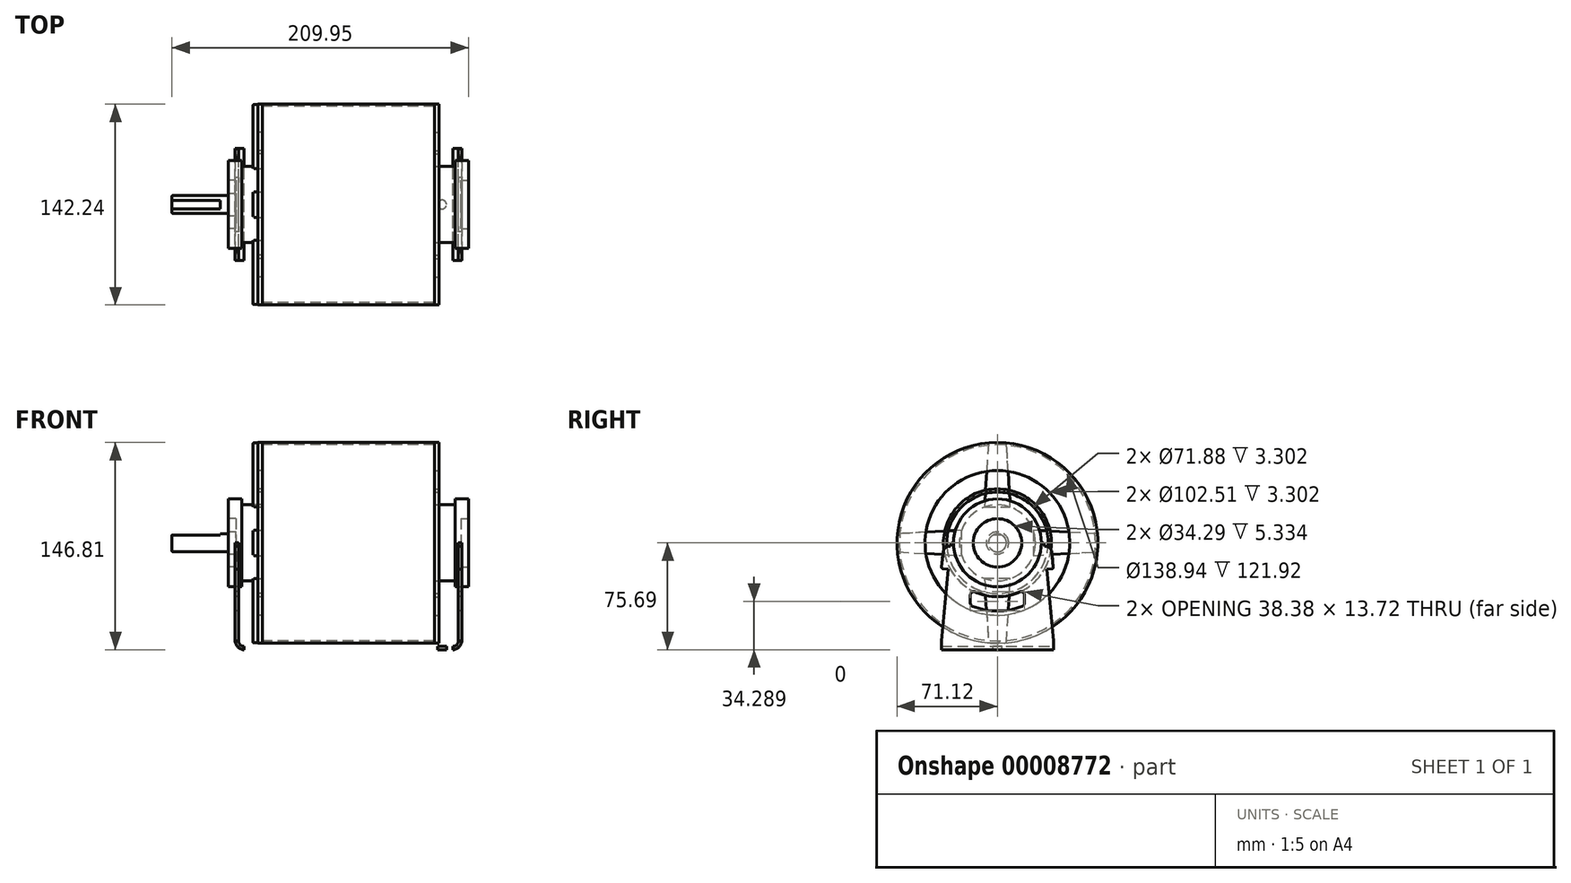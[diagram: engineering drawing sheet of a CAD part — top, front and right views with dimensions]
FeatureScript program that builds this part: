
annotation { "Feature Type Name" : "Feature", "Feature Type Description" : "" }
export const myFeature = defineFeature(function(context is Context, id is Id, definition is map)
    precondition{}
    {
        {
            var Q0;
            Q0=qCreatedBy(makeId("Right.planeOp"),FACE);
            var sketch = newSketch(context, id + "F0", { "sketchPlane" : qUnion([Q0])});
            skCircle(sketch, "E0", {"center": v(0, 0) * mm, "radius": 71.12 * mm});
            skCircle(sketch, "E1.0", {"center": v(0, 0) * mm, "radius": 69.47 * mm});
            skSolve(sketch);
        }
        {
            var Q0;
            Q0=makeQuery(id+"F0.imprint","IMPRINT",FACE,{"disambiguationData":[TD([[makeQuery(id+"F0.imprint","IMPRINT",EDGE,{"derivedFrom":sQuery(id+"F0.wireOp",EDGE,"E0")}),1.0]])]});
            extrude(context, id + "F1", {"entities" : qUnion([Q0]), "depth" : 121.92 * mm});
        }
        {
            var Q0;
            Q0=qCreatedBy(makeId("Front.planeOp"),FACE);
            var sketch = newSketch(context, id + "F2", { "sketchPlane" : qUnion([Q0])});
            skLineSegment(sketch, "E2", {"start": v(0, 0) * mm, "end": v(0, 71.12) * mm});
            skLineSegment(sketch, "E3", {"start": v(0, 71.12) * mm, "end": v(-3.3, 71.12) * mm});
            skLineSegment(sketch, "E4", {"start": v(-3.3, 71.12) * mm, "end": v(-3.3, 26.92) * mm});
            skLineSegment(sketch, "E5", {"start": v(-3.3, 26.92) * mm, "end": v(-14.48, 26.92) * mm});
            skLineSegment(sketch, "E6", {"start": v(-14.48, 26.92) * mm, "end": v(-14.48, 31.12) * mm});
            skLineSegment(sketch, "E7", {"start": v(-14.48, 31.12) * mm, "end": v(-24, 31.12) * mm});
            skLineSegment(sketch, "E8", {"start": v(-24, 31.12) * mm, "end": v(-24, 17.15) * mm});
            skLineSegment(sketch, "E9", {"start": v(-24, 17.15) * mm, "end": v(-18.67, 17.15) * mm});
            skLineSegment(sketch, "E10", {"start": v(-18.67, 17.15) * mm, "end": v(-18.67, 0) * mm});
            skLineSegment(sketch, "E11", {"start": v(-18.67, 0) * mm, "end": v(0, 0) * mm});
            skSolve(sketch);
        }
        {
            var Q0;
            Q0=makeQuery(id+"F2.imprint","IMPRINT",FACE,{"disambiguationData":[TD([[makeQuery(id+"F2.imprint","IMPRINT",EDGE,{"derivedFrom":sQuery(id+"F2.wireOp",EDGE,"E2")}),1.0]])]});
            var Q1;
            Q1=sQuery(id+"F2.wireOp",EDGE,"E11");
            revolve(context, id + "F3", {"entities" : qUnion([Q0]), "axis" : qUnion([Q1]), "revolveType" : RevolveType.FULL});
        }
        {
            var Q0;
            Q0=makeQuery(id+"F3.opRevolve","SWEPT_FACE",FACE,{"disambiguationData":[OSD([sQuery(id+"F2.wireOp",EDGE,"E4")])]});
            var sketch = newSketch(context, id + "F4", { "sketchPlane" : qUnion([Q0])});
            skCircle(sketch, "E12", {"center": v(0, 0) * mm, "radius": 51.26 * mm});
            skCircle(sketch, "E13", {"center": v(0, 0) * mm, "radius": 38.23 * mm});
            skCircle(sketch, "E14.0", {"center": v(0, 0) * mm, "radius": 35.94 * mm});
            skSolve(sketch);
        }
        {
            var Q0;
            Q0 = qSketchRegion(id + "F4", true);
            var Q1;
            Q1=makeQuery(id+"F4.imprint","IMPRINT",FACE,{"disambiguationData":[TD([[makeQuery(id+"F4.imprint","IMPRINT",EDGE,{"derivedFrom":sQuery(id+"F4.wireOp",EDGE,"E14.0")}),1.0]])]});
            extrude(context, id + "F5", {"entities" : qUnion([Q0, Q1]), "operationType" : NewBodyOperationType.REMOVE, "endBound" : BoundingType.THROUGH_ALL, "oppositeDirection" : true, "depth" : 25.4 * mm});
        }
        {
            var Q0;
            Q0=qCreatedBy(makeId("Right.planeOp"),FACE);
            var sketch = newSketch(context, id + "F6", { "sketchPlane" : qUnion([Q0])});
            skLineSegment(sketch, "E15", {"start": v(0, 0) * mm, "end": v(0, 71.12) * mm, "construction": true});
            skPoint(sketch, "E16.rect.middle", {"position": v(0, 71.12) * mm});
            skCircle(sketch, "E17", {"center": v(0, 26.92) * mm, "radius": 9.2 * mm, "construction": true});
            skCircle(sketch, "E18.0", {"center": v(0, 0) * mm, "radius": 71.12 * mm, "construction": true});
            skCircle(sketch, "E19", {"center": v(0, 71.12) * mm, "radius": 6.35 * mm, "construction": true});
            skLineSegment(sketch, "E20", {"start": v(9.07, 25.35) * mm, "end": v(6.38, 70.83) * mm});
            skLineSegment(sketch, "E21", {"start": v(6.38, 70.83) * mm, "end": v(-6.38, 70.83) * mm});
            skLineSegment(sketch, "E22", {"start": v(-6.38, 70.83) * mm, "end": v(-9.07, 25.35) * mm});
            skLineSegment(sketch, "E23", {"start": v(-9.07, 25.35) * mm, "end": v(9.07, 25.35) * mm});
            skCircle(sketch, "E24.0", {"center": v(0, 0) * mm, "radius": 26.92 * mm, "construction": true});
            skSolve(sketch);
        }
        {
            var Q0;
            {var subQ3=sQuery(id+"F6.wireOp",EDGE,"E20");Q0=makeQuery(id+"F6.imprint","IMPRINT",FACE,{"disambiguationData":[TD([[makeQuery(id+"F6.imprint","IMPRINT",EDGE,{"derivedFrom":subQ3}),1.0]])]});}
            extrude(context, id + "F7", {"entities" : qUnion([Q0]), "oppositeDirection" : true, "depth" : 6.6 * mm});
        }
        {
            var Q0;
            Q0=makeQuery(id+"F7.opExtrude","CAP_EDGE",EDGE,{"disambiguationData":[OSD([sQuery(id+"F6.wireOp",EDGE,"E20")])],"isStart":false});
            var Q1;
            Q1=makeQuery(id+"F7.opExtrude","CAP_EDGE",EDGE,{"disambiguationData":[OSD([sQuery(id+"F6.wireOp",EDGE,"E21")])],"isStart":false});
            var Q2;
            Q2=makeQuery(id+"F7.opExtrude","CAP_EDGE",EDGE,{"disambiguationData":[OSD([sQuery(id+"F6.wireOp",EDGE,"E22")])],"isStart":false});
            var Q3;
            Q3=makeQuery(id+"F7.opExtrude","SWEPT_EDGE",EDGE,{"disambiguationData":[OSD([sQuery(id+"F2.wireOp",EDGE,"E3"),sQuery(id+"F2.wireOp",EDGE,"E4"),sQuery(id+"F6.wireOp",EDGE,"E20"),sQuery(id+"F6.wireOp",EDGE,"E21")])]});
            var Q4;
            Q4=makeQuery(id+"F7.opExtrude","SWEPT_EDGE",EDGE,{"disambiguationData":[OSD([sQuery(id+"F2.wireOp",EDGE,"E3"),sQuery(id+"F2.wireOp",EDGE,"E4"),sQuery(id+"F6.wireOp",EDGE,"E21"),sQuery(id+"F6.wireOp",EDGE,"E22")])]});
            fillet(context, id + "F8", {"entities" : qUnion([Q0, Q1, Q2, Q3, Q4]), "radius" : 0.5 * mm, "tangentPropagation" : true, "allowEdgeOverflow" : false});
        }
        {
            var Q0;
            Q0=makeQuery(id+"F7.opExtrude","SWEPT_BODY",BODY,{"disambiguationData":[OSD([sQuery(id+"F2.wireOp",EDGE,"E4"),sQuery(id+"F2.wireOp",EDGE,"E5"),sQuery(id+"F6.wireOp",EDGE,"E20"),sQuery(id+"F6.wireOp",EDGE,"E21"),sQuery(id+"F6.wireOp",EDGE,"E22")])]});
            var Q1;
            Q1=sQuery(id+"F2.wireOp",EDGE,"E11");
            circularPattern(context, id + "F9", {"entities" : qUnion([Q0]), "axis" : qUnion([Q1]), "angle" : 360 * degree, "instanceCount" : 4, "equalSpace" : true});
        }
        {
            var Q0;
            Q0=qCreatedBy(makeId("Right.planeOp"),FACE);
            cPlane(context, id + "F10", {"entities" : qUnion([Q0]), "cplaneType" : CPlaneType.OFFSET, "offset" : 60.96 * mm, "width" : 152.4 * mm, "height" : 152.4 * mm});
        }
        {
            var Q0;
            Q0=makeQuery(id+"F5.boolean.opBoolean","SPLIT",BODY,{"disambiguationData":[OD(0.0)],"derivedFrom":makeQuery(id+"F3.opRevolve","SWEPT_BODY",BODY,{"disambiguationData":[OSD([sQuery(id+"F2.wireOp",EDGE,"E2"),sQuery(id+"F2.wireOp",EDGE,"E3"),sQuery(id+"F2.wireOp",EDGE,"E4"),sQuery(id+"F2.wireOp",EDGE,"E5"),sQuery(id+"F2.wireOp",EDGE,"E6"),sQuery(id+"F2.wireOp",EDGE,"E7"),sQuery(id+"F2.wireOp",EDGE,"E8"),sQuery(id+"F2.wireOp",EDGE,"E9"),sQuery(id+"F2.wireOp",EDGE,"E10"),sQuery(id+"F2.wireOp",EDGE,"E11")])]})});
            var Q1;
            Q1=qCreatedBy(id+"F10.planeOp",FACE);
            mirror(context, id + "F11", {"entities" : qUnion([Q0]), "mirrorPlane" : qUnion([Q1])});
        }
        {
            var Q0;
            Q0=qCreatedBy(makeId("Front.planeOp"),FACE);
            var sketch = newSketch(context, id + "F12", { "sketchPlane" : qUnion([Q0])});
            skLineSegment(sketch, "E25.0.0", {"start": v(-18.67, -17.15) * mm, "end": v(-18.67, 17.15) * mm, "construction": true});
            skLineSegment(sketch, "E26", {"start": v(-18.67, 0) * mm, "end": v(-64.03, 0) * mm});
            skLineSegment(sketch, "E27", {"start": v(-64.03, 0) * mm, "end": v(-64.03, 5.84) * mm});
            skLineSegment(sketch, "E28", {"start": v(-63.53, 6.35) * mm, "end": v(-23.75, 6.35) * mm});
            skLineSegment(sketch, "E29", {"start": v(-23.24, 7.89) * mm, "end": v(-18.67, 7.89) * mm});
            skLineSegment(sketch, "E30", {"start": v(-18.67, 7.89) * mm, "end": v(-18.67, 0) * mm});
            skLineSegment(sketch, "E31", {"start": v(-23.75, 7.38) * mm, "end": v(-23.75, 6.35) * mm});
            skPoint(sketch, "E32.visualSharp", {"position": v(-23.75, 7.89) * mm});
            skArc(sketch, "E32.filletArc", {"start": v(-23.24, 7.89) * mm, "mid": v(-23.6, 7.74) * mm, "end": v(-23.75, 7.38) * mm});
            skPoint(sketch, "E33.visualSharp", {"position": v(-64.03, 6.35) * mm});
            skArc(sketch, "E33.filletArc", {"start": v(-63.53, 6.35) * mm, "mid": v(-63.88, 6.2) * mm, "end": v(-64.03, 5.84) * mm});
            skSolve(sketch);
        }
        {
            var Q0;
            Q0=makeQuery(id+"F12.imprint","IMPRINT",FACE,{"disambiguationData":[TD([[makeQuery(id+"F12.imprint","IMPRINT",EDGE,{"derivedFrom":sQuery(id+"F12.wireOp",EDGE,"E26")}),-1.0]])]});
            var Q1;
            Q1=sQuery(id+"F12.wireOp",EDGE,"E26");
            revolve(context, id + "F13", {"entities" : qUnion([Q0]), "axis" : qUnion([Q1]), "revolveType" : RevolveType.FULL});
        }
        {
            var Q0;
            Q0=makeQuery(id+"F13.opRevolve","SWEPT_FACE",FACE,{"disambiguationData":[OSD([sQuery(id+"F12.wireOp",EDGE,"E27")])]});
            var sketch = newSketch(context, id + "F14", { "sketchPlane" : qUnion([Q0])});
            skCircle(sketch, "E34.0", {"center": v(0, 0) * mm, "radius": 6.35 * mm});
            skLineSegment(sketch, "E35", {"start": v(-6.6, -6.35) * mm, "end": v(6.6, -6.35) * mm, "construction": true});
            skLineSegment(sketch, "E36", {"start": v(0, -6.35) * mm, "end": v(0, 6.35) * mm, "construction": true});
            skLineSegment(sketch, "E37.0", {"start": v(-3.02, 5.59) * mm, "end": v(3.02, 5.59) * mm});
            skSolve(sketch);
        }
        {
            var Q0;
            {var subQ0=makeQuery(id+"F13.opRevolve","SWEPT_EDGE",EDGE,{"disambiguationData":[OSD([sQuery(id+"F12.wireOp",EDGE,"E27"),sQuery(id+"F12.wireOp",EDGE,"E33.filletArc")])]});var subQ1=sQuery(id+"F14.wireOp",EDGE,"E37.0");var subQ3=makeQuery(id+"F14.imprint","INTERSECT",VERTEX,{"disambiguationData":[OD(0.0)],"derivedFrom":[subQ0,subQ1]});Q0=makeQuery(id+"F14.imprint","IMPRINT",FACE,{"disambiguationData":[TD([[makeQuery(id+"F14.imprint","IMPRINT",EDGE,{"disambiguationData":[TD([[subQ3,-1.0]])],"derivedFrom":subQ1}),1.0]])]});}
            var Q1;
            {var subQ1=sQuery(id+"F14.wireOp",EDGE,"E37.0");var subQ4=sQuery(id+"F14.wireOp",EDGE,"E34.0");var subQ6=makeQuery(id+"F14.imprint","INTERSECT",VERTEX,{"disambiguationData":[OD(0.0)],"derivedFrom":[subQ4,subQ1]});Q1=makeQuery(id+"F14.imprint","IMPRINT",FACE,{"disambiguationData":[TD([[makeQuery(id+"F14.imprint","IMPRINT",EDGE,{"disambiguationData":[TD([[subQ6,1.0]])],"derivedFrom":subQ4}),1.0]])]});}
            extrude(context, id + "F15", {"entities" : qUnion([Q0, Q1]), "operationType" : NewBodyOperationType.REMOVE, "oppositeDirection" : true, "depth" : 34.04 * mm});
        }
        {
            var Q0;
            Q0=qCreatedBy(makeId("Front.planeOp"),FACE);
            var sketch = newSketch(context, id + "F16", { "sketchPlane" : qUnion([Q0])});
            skLineSegment(sketch, "E38", {"start": v(-154.25, 0) * mm, "end": v(252.33, 0) * mm, "construction": true});
            skLineSegment(sketch, "E39", {"start": v(-12.9, -75.7) * mm, "end": v(134.81, -75.7) * mm});
            skLineSegment(sketch, "E40", {"start": v(-24, 31.12) * mm, "end": v(-14.48, 31.12) * mm, "construction": true});
            skLineSegment(sketch, "E41", {"start": v(136.4, 31.12) * mm, "end": v(145.92, 31.12) * mm, "construction": true});
            skLineSegment(sketch, "E42", {"start": v(-19.24, 31.12) * mm, "end": v(-19.24, 0) * mm, "construction": true});
            skLineSegment(sketch, "E43", {"start": v(141.16, 31.12) * mm, "end": v(141.16, 0) * mm, "construction": true});
            skLineSegment(sketch, "E44", {"start": v(-19.24, 0) * mm, "end": v(-19.24, -69.34) * mm});
            skLineSegment(sketch, "E45", {"start": v(141.16, 0) * mm, "end": v(141.16, -69.34) * mm});
            skPoint(sketch, "E46.visualSharp", {"position": v(-19.24, -75.7) * mm});
            skArc(sketch, "E46.filletArc", {"start": v(-19.24, -69.34) * mm, "mid": v(-17.38, -73.83) * mm, "end": v(-12.9, -75.7) * mm});
            skPoint(sketch, "E47.visualSharp", {"position": v(141.16, -75.7) * mm});
            skArc(sketch, "E47.filletArc", {"start": v(134.81, -75.7) * mm, "mid": v(139.3, -73.83) * mm, "end": v(141.16, -69.34) * mm});
            skLineSegment(sketch, "E48.0", {"start": v(138.87, 0) * mm, "end": v(138.87, -69.34) * mm});
            skArc(sketch, "E48.1", {"start": v(134.81, -73.4) * mm, "mid": v(137.68, -72.22) * mm, "end": v(138.87, -69.34) * mm});
            skLineSegment(sketch, "E48.2", {"start": v(-12.9, -73.4) * mm, "end": v(134.81, -73.4) * mm});
            skArc(sketch, "E48.3", {"start": v(-16.95, -69.34) * mm, "mid": v(-15.76, -72.22) * mm, "end": v(-12.9, -73.4) * mm});
            skLineSegment(sketch, "E48.4", {"start": v(-16.95, 0) * mm, "end": v(-16.95, -69.34) * mm});
            skLineSegment(sketch, "E49", {"start": v(-19.24, 0) * mm, "end": v(-16.95, 0) * mm});
            skLineSegment(sketch, "E50", {"start": v(138.87, 0) * mm, "end": v(141.16, 0) * mm});
            skSolve(sketch);
        }
        {
            var Q0;
            Q0 = qSketchRegion(id + "F16", true);
            extrude(context, id + "F17", {"entities" : qUnion([Q0]), "depth" : 79.5 * mm, "symmetric" : true});
        }
        {
            var Q0;
            Q0=qCreatedBy(makeId("Top.planeOp"),FACE);
            cPlane(context, id + "F18", {"entities" : qUnion([Q0]), "cplaneType" : CPlaneType.OFFSET, "offset" : 75.7 * mm, "oppositeDirection" : true, "width" : 152.4 * mm, "height" : 152.4 * mm});
        }
        {
            var Q0;
            Q0=qCreatedBy(id+"F18.planeOp",FACE);
            var sketch = newSketch(context, id + "F19", { "sketchPlane" : qUnion([Q0])});
            skLineSegment(sketch, "E51.0", {"start": v(-19.24, -39.75) * mm, "end": v(-12.9, -39.75) * mm, "construction": true});
            skLineSegment(sketch, "E52.0", {"start": v(-19.24, 39.75) * mm, "end": v(-12.9, 39.75) * mm, "construction": true});
            skLineSegment(sketch, "E53.bottom", {"start": v(15.34, 66.04) * mm, "end": v(15.34, 66.04) * mm});
            skLineSegment(sketch, "E53.top", {"start": v(15.34, 40.64) * mm, "end": v(15.34, 40.64) * mm});
            skLineSegment(sketch, "E53.left", {"start": v(11.37, 62.07) * mm, "end": v(11.37, 44.6) * mm});
            skLineSegment(sketch, "E53.right", {"start": v(19.3, 62.07) * mm, "end": v(19.3, 44.6) * mm});
            skPoint(sketch, "E54.visualSharp", {"position": v(11.37, 66.04) * mm});
            skArc(sketch, "E54.filletArc", {"start": v(15.34, 66.04) * mm, "mid": v(12.53, 64.88) * mm, "end": v(11.37, 62.07) * mm});
            skPoint(sketch, "E55.visualSharp", {"position": v(19.3, 66.04) * mm});
            skArc(sketch, "E55.filletArc", {"start": v(19.3, 62.07) * mm, "mid": v(18.14, 64.88) * mm, "end": v(15.34, 66.04) * mm});
            skPoint(sketch, "E56.visualSharp", {"position": v(19.3, 40.64) * mm});
            skArc(sketch, "E56.filletArc", {"start": v(15.34, 40.64) * mm, "mid": v(18.14, 41.8) * mm, "end": v(19.3, 44.6) * mm});
            skPoint(sketch, "E57.visualSharp", {"position": v(11.37, 40.64) * mm});
            skArc(sketch, "E57.filletArc", {"start": v(11.37, 44.6) * mm, "mid": v(12.53, 41.8) * mm, "end": v(15.34, 40.64) * mm});
            skLineSegment(sketch, "E58", {"start": v(2.98, 39.75) * mm, "end": v(2.98, -39.75) * mm, "construction": true});
            skLineSegment(sketch, "E59", {"start": v(-19.24, 0) * mm, "end": v(141.16, 0) * mm, "construction": true});
            skLineSegment(sketch, "E60", {"start": v(9.33, 71.5) * mm, "end": v(111.68, 71.5) * mm});
            skLineSegment(sketch, "E61", {"start": v(9.33, -71.5) * mm, "end": v(111.68, -71.5) * mm});
            skLineSegment(sketch, "E62", {"start": v(2.98, 46.1) * mm, "end": v(2.98, 65.15) * mm});
            skLineSegment(sketch, "E63", {"start": v(2.98, -46.1) * mm, "end": v(2.98, -65.15) * mm});
            skLineSegment(sketch, "E64", {"start": v(-19.24, 39.75) * mm, "end": v(-19.24, -39.75) * mm, "construction": true});
            skLineSegment(sketch, "E65.0", {"start": v(141.16, -39.75) * mm, "end": v(141.16, 39.75) * mm, "construction": true});
            skLineSegment(sketch, "E66", {"start": v(141.16, 39.75) * mm, "end": v(134.81, 39.75) * mm, "construction": true});
            skLineSegment(sketch, "E67", {"start": v(126.25, 45.4) * mm, "end": v(117.6, 67.47) * mm});
            skPoint(sketch, "E68.visualSharp", {"position": v(128.46, 39.75) * mm});
            skArc(sketch, "E68.filletArc", {"start": v(126.25, 45.4) * mm, "mid": v(129.51, 41.3) * mm, "end": v(134.52, 39.75) * mm});
            skPoint(sketch, "E69.visualSharp", {"position": v(2.98, 71.5) * mm});
            skArc(sketch, "E69.filletArc", {"start": v(9.33, 71.5) * mm, "mid": v(4.84, 69.64) * mm, "end": v(2.98, 65.15) * mm});
            skLineSegment(sketch, "E70.0.MirrorCS", {"start": v(141.16, -39.75) * mm, "end": v(134.81, -39.75) * mm, "construction": true});
            skLineSegment(sketch, "E70.1.MirrorCS", {"start": v(126.25, -45.4) * mm, "end": v(117.6, -67.47) * mm});
            skArc(sketch, "E70.2.MirrorCS", {"start": v(126.25, -45.4) * mm, "mid": v(129.51, -41.3) * mm, "end": v(134.52, -39.75) * mm});
            skPoint(sketch, "E71.visualSharp", {"position": v(116.01, 71.5) * mm});
            skArc(sketch, "E71.filletArc", {"start": v(117.6, 67.47) * mm, "mid": v(115.26, 70.4) * mm, "end": v(111.68, 71.5) * mm});
            skPoint(sketch, "E72.visualSharp", {"position": v(116.01, -71.5) * mm});
            skArc(sketch, "E72.filletArc", {"start": v(111.68, -71.5) * mm, "mid": v(115.26, -70.4) * mm, "end": v(117.6, -67.47) * mm});
            skPoint(sketch, "E73.visualSharp", {"position": v(2.98, -71.5) * mm});
            skArc(sketch, "E73.filletArc", {"start": v(2.98, -65.15) * mm, "mid": v(4.84, -69.64) * mm, "end": v(9.33, -71.5) * mm});
            skPoint(sketch, "E74.visualSharp", {"position": v(2.98, 39.75) * mm});
            skArc(sketch, "E74.filletArc", {"start": v(-3.37, 39.75) * mm, "mid": v(1.12, 41.61) * mm, "end": v(2.98, 46.1) * mm});
            skPoint(sketch, "E75.visualSharp", {"position": v(2.98, -39.75) * mm});
            skArc(sketch, "E75.filletArc", {"start": v(2.98, -46.1) * mm, "mid": v(1.12, -41.61) * mm, "end": v(-3.37, -39.75) * mm});
            skArc(sketch, "E76.0.1.0", {"start": v(15.34, -66.04) * mm, "mid": v(18.14, -64.88) * mm, "end": v(19.3, -62.07) * mm});
            skArc(sketch, "E76.0.1.1", {"start": v(11.37, -62.07) * mm, "mid": v(12.53, -64.88) * mm, "end": v(15.34, -66.04) * mm});
            skLineSegment(sketch, "E76.0.1.2", {"start": v(11.37, -44.6) * mm, "end": v(11.37, -62.07) * mm});
            skArc(sketch, "E76.0.1.3", {"start": v(15.34, -40.64) * mm, "mid": v(12.53, -41.8) * mm, "end": v(11.37, -44.6) * mm});
            skArc(sketch, "E76.0.1.4", {"start": v(19.3, -44.6) * mm, "mid": v(18.14, -41.8) * mm, "end": v(15.34, -40.64) * mm});
            skLineSegment(sketch, "E76.0.1.5", {"start": v(19.3, -44.6) * mm, "end": v(19.3, -62.07) * mm});
            skArc(sketch, "E76.1.0.0", {"start": v(83.92, 40.64) * mm, "mid": v(86.72, 41.8) * mm, "end": v(87.88, 44.6) * mm});
            skArc(sketch, "E76.1.0.1", {"start": v(79.95, 44.6) * mm, "mid": v(81.1, 41.8) * mm, "end": v(83.92, 40.64) * mm});
            skLineSegment(sketch, "E76.1.0.2", {"start": v(79.95, 62.07) * mm, "end": v(79.95, 44.6) * mm});
            skArc(sketch, "E76.1.0.3", {"start": v(83.92, 66.04) * mm, "mid": v(81.1, 64.88) * mm, "end": v(79.95, 62.07) * mm});
            skArc(sketch, "E76.1.0.4", {"start": v(87.88, 62.07) * mm, "mid": v(86.72, 64.88) * mm, "end": v(83.92, 66.04) * mm});
            skLineSegment(sketch, "E76.1.0.5", {"start": v(87.88, 62.07) * mm, "end": v(87.88, 44.6) * mm});
            skArc(sketch, "E76.1.1.0", {"start": v(83.92, -66.04) * mm, "mid": v(86.72, -64.88) * mm, "end": v(87.88, -62.07) * mm});
            skArc(sketch, "E76.1.1.1", {"start": v(79.95, -62.07) * mm, "mid": v(81.1, -64.88) * mm, "end": v(83.92, -66.04) * mm});
            skLineSegment(sketch, "E76.1.1.2", {"start": v(79.95, -44.6) * mm, "end": v(79.95, -62.07) * mm});
            skArc(sketch, "E76.1.1.3", {"start": v(83.92, -40.64) * mm, "mid": v(81.1, -41.8) * mm, "end": v(79.95, -44.6) * mm});
            skArc(sketch, "E76.1.1.4", {"start": v(87.88, -44.6) * mm, "mid": v(86.72, -41.8) * mm, "end": v(83.92, -40.64) * mm});
            skLineSegment(sketch, "E76.1.1.5", {"start": v(87.88, -44.6) * mm, "end": v(87.88, -62.07) * mm});
            skLineSegment(sketch, "E76.direction1", {"start": v(15.34, 40.64) * mm, "end": v(83.92, 40.64) * mm, "construction": true});
            skLineSegment(sketch, "E76.direction2", {"start": v(15.34, 40.64) * mm, "end": v(15.34, -66.04) * mm, "construction": true});
            skLineSegment(sketch, "E77.0", {"start": v(-12.9, -39.75) * mm, "end": v(-12.9, 39.75) * mm});
            skLineSegment(sketch, "E78.0", {"start": v(134.81, -39.75) * mm, "end": v(134.81, 39.75) * mm});
            skLineSegment(sketch, "E79", {"start": v(-12.9, 39.75) * mm, "end": v(-3.37, 39.75) * mm});
            skLineSegment(sketch, "E80", {"start": v(-12.9, -39.75) * mm, "end": v(-3.37, -39.75) * mm});
            skLineSegment(sketch, "E81", {"start": v(134.81, 39.75) * mm, "end": v(134.52, 39.75) * mm});
            skLineSegment(sketch, "E82", {"start": v(134.81, -39.75) * mm, "end": v(134.52, -39.75) * mm});
            skSolve(sketch);
        }
        {
            var Q0;
            Q0=makeQuery(id+"F19.imprint","IMPRINT",FACE,{"disambiguationData":[TD([[makeQuery(id+"F19.imprint","IMPRINT",EDGE,{"derivedFrom":sQuery(id+"F19.wireOp",EDGE,"E53.left")}),-1.0]])]});
            extrude(context, id + "F20", {"entities" : qUnion([Q0]), "operationType" : NewBodyOperationType.ADD, "depth" : 2.3 * mm});
        }
        {
            var Q0;
            Q0=makeQuery(id+"F17.opExtrude","SWEPT_FACE",FACE,{"disambiguationData":[OSD([sQuery(id+"F16.wireOp",EDGE,"E44")])]});
            var sketch = newSketch(context, id + "F21", { "sketchPlane" : qUnion([Q0])});
            skArc(sketch, "E83.0", {"start": v(-31.12, 0) * mm, "mid": v(0, -31.12) * mm, "end": v(31.12, 0) * mm});
            skLineSegment(sketch, "E84.0", {"start": v(39.75, -69.34) * mm, "end": v(-39.75, -69.34) * mm});
            skLineSegment(sketch, "E85", {"start": v(31.87, 0) * mm, "end": v(31.12, 0) * mm});
            skLineSegment(sketch, "E86", {"start": v(-33.13, -1.15) * mm, "end": v(-39.75, -69.34) * mm});
            skLineSegment(sketch, "E87", {"start": v(33.13, -1.15) * mm, "end": v(39.75, -69.34) * mm});
            skPoint(sketch, "E88.end.orphan", {"position": v(-39.75, 0) * mm});
            skPoint(sketch, "E89.0.start.orphan", {"position": v(39.75, 0) * mm});
            skLineSegment(sketch, "E90.trimOffspring", {"start": v(-31.12, 0) * mm, "end": v(-31.87, 0) * mm});
            skLineSegment(sketch, "E91", {"start": v(0, 0) * mm, "end": v(0, -69.34) * mm, "construction": true});
            skPoint(sketch, "E92.visualSharp", {"position": v(-33.02, 0) * mm});
            skArc(sketch, "E92.filletArc", {"start": v(-31.87, 0) * mm, "mid": v(-32.72, -0.33) * mm, "end": v(-33.13, -1.15) * mm});
            skPoint(sketch, "E93.visualSharp", {"position": v(33.02, 0) * mm});
            skArc(sketch, "E93.filletArc", {"start": v(33.13, -1.15) * mm, "mid": v(32.72, -0.33) * mm, "end": v(31.87, 0) * mm});
            skLineSegment(sketch, "E94.bottom", {"start": v(33.27, -2.6) * mm, "end": v(33.78, -2.55) * mm});
            skLineSegment(sketch, "E94.top", {"start": v(34.84, -18.78) * mm, "end": v(38.38, -18.44) * mm});
            skLineSegment(sketch, "E94.left", {"start": v(33.27, -2.6) * mm, "end": v(34.84, -18.78) * mm});
            skLineSegment(sketch, "E94.right", {"start": v(38.5, -6.43) * mm, "end": v(39.52, -17.05) * mm});
            skPoint(sketch, "E95.visualSharp", {"position": v(38.08, -2.13) * mm});
            skArc(sketch, "E95.filletArc", {"start": v(38.5, -6.43) * mm, "mid": v(36.94, -3.51) * mm, "end": v(33.78, -2.55) * mm});
            skPoint(sketch, "E96.visualSharp", {"position": v(39.65, -18.31) * mm});
            skArc(sketch, "E96.filletArc", {"start": v(38.38, -18.44) * mm, "mid": v(39.24, -17.98) * mm, "end": v(39.52, -17.05) * mm});
            skLineSegment(sketch, "E97.0.MirrorCS", {"start": v(-33.27, -2.6) * mm, "end": v(-33.78, -2.55) * mm});
            skArc(sketch, "E97.1.MirrorCS", {"start": v(-38.5, -6.43) * mm, "mid": v(-36.94, -3.51) * mm, "end": v(-33.78, -2.55) * mm});
            skLineSegment(sketch, "E97.2.MirrorCS", {"start": v(-34.84, -18.78) * mm, "end": v(-38.38, -18.44) * mm});
            skLineSegment(sketch, "E97.3.MirrorCS", {"start": v(-38.5, -6.43) * mm, "end": v(-39.52, -17.05) * mm});
            skArc(sketch, "E97.4.MirrorCS", {"start": v(-38.38, -18.44) * mm, "mid": v(-39.24, -17.98) * mm, "end": v(-39.52, -17.05) * mm});
            skArc(sketch, "E98", {"start": v(-15.6, -34.76) * mm, "mid": v(0, -38.1) * mm, "end": v(15.6, -34.76) * mm});
            skArc(sketch, "E99.0", {"start": v(-17.57, -44.95) * mm, "mid": v(0, -48.26) * mm, "end": v(17.57, -44.95) * mm});
            skLineSegment(sketch, "E100.rect.left", {"start": v(19.19, -37.07) * mm, "end": v(19.19, -42.58) * mm});
            skLineSegment(sketch, "E100.rect.right", {"start": v(-19.19, -37.07) * mm, "end": v(-19.19, -42.58) * mm});
            skPoint(sketch, "E100.rect.middle", {"position": v(0, -43.18) * mm});
            skPoint(sketch, "E101.orphan", {"position": v(-19.19, -53.44) * mm});
            skPoint(sketch, "E100.rect.top.start.orphan", {"position": v(19.19, -53.44) * mm});
            skPoint(sketch, "E102.visualSharp", {"position": v(-19.19, -44.28) * mm});
            skArc(sketch, "E102.filletArc", {"start": v(-19.19, -42.58) * mm, "mid": v(-18.75, -44.01) * mm, "end": v(-17.57, -44.95) * mm});
            skPoint(sketch, "E103.visualSharp", {"position": v(19.19, -44.28) * mm});
            skArc(sketch, "E103.filletArc", {"start": v(17.57, -44.95) * mm, "mid": v(18.75, -44.01) * mm, "end": v(19.19, -42.58) * mm});
            skPoint(sketch, "E104.visualSharp", {"position": v(19.19, -32.92) * mm});
            skArc(sketch, "E104.filletArc", {"start": v(19.19, -37.07) * mm, "mid": v(18.03, -34.94) * mm, "end": v(15.6, -34.76) * mm});
            skPoint(sketch, "E105.visualSharp", {"position": v(-19.19, -32.92) * mm});
            skArc(sketch, "E105.filletArc", {"start": v(-15.6, -34.76) * mm, "mid": v(-18.03, -34.94) * mm, "end": v(-19.19, -37.07) * mm});
            skSolve(sketch);
        }
        {
            var Q0;
            {var subQ2=sQuery(id+"F21.wireOp",EDGE,"E92.filletArc");Q0=makeQuery(id+"F21.imprint","IMPRINT",FACE,{"disambiguationData":[TD([[makeQuery(id+"F21.imprint","IMPRINT",EDGE,{"derivedFrom":subQ2}),-1.0]])]});}
            var Q1;
            {var subQ2=sQuery(id+"F21.wireOp",EDGE,"E93.filletArc");Q1=makeQuery(id+"F21.imprint","IMPRINT",FACE,{"disambiguationData":[TD([[makeQuery(id+"F21.imprint","IMPRINT",EDGE,{"derivedFrom":subQ2}),-1.0]])]});}
            var Q2;
            {var subQ1=sQuery(id+"F21.wireOp",EDGE,"E83.0");Q2=makeQuery(id+"F21.imprint","IMPRINT",FACE,{"disambiguationData":[TD([[makeQuery(id+"F21.imprint","IMPRINT",EDGE,{"derivedFrom":subQ1}),1.0]])]});}
            var Q3;
            Q3=makeQuery(id+"F21.imprint","IMPRINT",FACE,{"disambiguationData":[TD([[makeQuery(id+"F21.imprint","IMPRINT",EDGE,{"derivedFrom":sQuery(id+"F21.wireOp",EDGE,"E98")}),-1.0]])]});
            extrude(context, id + "F22", {"entities" : qUnion([Q0, Q1, Q2, Q3]), "oppositeDirection" : true, "depth" : 160.4 * mm});
        }
        {
            var Q0;
            Q0=makeQuery(id+"F22.opExtrude","SWEPT_BODY",BODY,{"disambiguationData":[OSD([sQuery(id+"F16.wireOp",EDGE,"E44"),sQuery(id+"F16.wireOp",EDGE,"E49"),sQuery(id+"F21.wireOp",EDGE,"E83.0")])]});
            var Q1;
            Q1=makeQuery(id+"F22.opExtrude","SWEPT_BODY",BODY,{"disambiguationData":[OSD([sQuery(id+"F16.wireOp",EDGE,"E44"),sQuery(id+"F16.wireOp",EDGE,"E49"),sQuery(id+"F21.wireOp",EDGE,"E86"),sQuery(id+"F21.wireOp",EDGE,"E92.filletArc"),sQuery(id+"F21.wireOp",EDGE,"E97.0.MirrorCS"),sQuery(id+"F21.wireOp",EDGE,"E97.1.MirrorCS"),sQuery(id+"F21.wireOp",EDGE,"E97.2.MirrorCS"),sQuery(id+"F21.wireOp",EDGE,"E97.3.MirrorCS"),sQuery(id+"F21.wireOp",EDGE,"E97.4.MirrorCS")])]});
            var Q2;
            Q2=makeQuery(id+"F22.opExtrude","SWEPT_BODY",BODY,{"disambiguationData":[OSD([sQuery(id+"F16.wireOp",EDGE,"E44"),sQuery(id+"F16.wireOp",EDGE,"E49"),sQuery(id+"F21.wireOp",EDGE,"E87"),sQuery(id+"F21.wireOp",EDGE,"E93.filletArc"),sQuery(id+"F21.wireOp",EDGE,"E94.bottom"),sQuery(id+"F21.wireOp",EDGE,"E94.top"),sQuery(id+"F21.wireOp",EDGE,"E94.right"),sQuery(id+"F21.wireOp",EDGE,"E95.filletArc"),sQuery(id+"F21.wireOp",EDGE,"E96.filletArc")])]});
            var Q3;
            Q3=makeQuery(id+"F22.opExtrude","SWEPT_BODY",BODY,{"disambiguationData":[OSD([sQuery(id+"F21.wireOp",EDGE,"E98"),sQuery(id+"F21.wireOp",EDGE,"E99.0"),sQuery(id+"F21.wireOp",EDGE,"E100.rect.left"),sQuery(id+"F21.wireOp",EDGE,"E100.rect.right"),sQuery(id+"F21.wireOp",EDGE,"E102.filletArc"),sQuery(id+"F21.wireOp",EDGE,"E103.filletArc"),sQuery(id+"F21.wireOp",EDGE,"E104.filletArc"),sQuery(id+"F21.wireOp",EDGE,"E105.filletArc")])]});
            var Q4;
            Q4=makeQuery(id+"F17.opExtrude","SWEPT_BODY",BODY,{"disambiguationData":[OSD([sQuery(id+"F16.wireOp",EDGE,"E39"),sQuery(id+"F16.wireOp",EDGE,"E44"),sQuery(id+"F16.wireOp",EDGE,"E45"),sQuery(id+"F16.wireOp",EDGE,"E46.filletArc"),sQuery(id+"F16.wireOp",EDGE,"E47.filletArc"),sQuery(id+"F16.wireOp",EDGE,"E48.0"),sQuery(id+"F16.wireOp",EDGE,"E48.1"),sQuery(id+"F16.wireOp",EDGE,"E48.2"),sQuery(id+"F16.wireOp",EDGE,"E48.3"),sQuery(id+"F16.wireOp",EDGE,"E48.4"),sQuery(id+"F16.wireOp",EDGE,"E49"),sQuery(id+"F16.wireOp",EDGE,"E50")])]});
            booleanBodies(context, id + "F23", {"operationType" : BooleanOperationType.SUBTRACTION, "tools" : qUnion([Q0, Q1, Q2, Q3]), "targets" : qUnion([Q4])});
        }
        {
            var Q0;
            Q0=makeQuery(id+"F20.boolean.opBoolean","MERGE",FACE,{"derivedFrom":[makeQuery(id+"F17.opExtrude","SWEPT_FACE",FACE,{"disambiguationData":[OSD([sQuery(id+"F16.wireOp",EDGE,"E48.2")])]}),makeQuery(id+"F20.opExtrude","CAP_FACE",FACE,{"disambiguationData":[OSD([sQuery(id+"F19.wireOp",EDGE,"E53.left"),sQuery(id+"F19.wireOp",EDGE,"E53.right"),sQuery(id+"F19.wireOp",EDGE,"E54.filletArc"),sQuery(id+"F19.wireOp",EDGE,"E55.filletArc"),sQuery(id+"F19.wireOp",EDGE,"E56.filletArc"),sQuery(id+"F19.wireOp",EDGE,"E57.filletArc"),sQuery(id+"F19.wireOp",EDGE,"E60"),sQuery(id+"F19.wireOp",EDGE,"E61"),sQuery(id+"F19.wireOp",EDGE,"E62"),sQuery(id+"F19.wireOp",EDGE,"E63"),sQuery(id+"F19.wireOp",EDGE,"E67"),sQuery(id+"F19.wireOp",EDGE,"E68.filletArc"),sQuery(id+"F19.wireOp",EDGE,"E69.filletArc"),sQuery(id+"F19.wireOp",EDGE,"E70.1.MirrorCS"),sQuery(id+"F19.wireOp",EDGE,"E70.2.MirrorCS"),sQuery(id+"F19.wireOp",EDGE,"E71.filletArc"),sQuery(id+"F19.wireOp",EDGE,"E72.filletArc"),sQuery(id+"F19.wireOp",EDGE,"E73.filletArc"),sQuery(id+"F19.wireOp",EDGE,"E74.filletArc"),sQuery(id+"F19.wireOp",EDGE,"E75.filletArc"),sQuery(id+"F19.wireOp",EDGE,"E76.0.1.0"),sQuery(id+"F19.wireOp",EDGE,"E76.0.1.1"),sQuery(id+"F19.wireOp",EDGE,"E76.0.1.2"),sQuery(id+"F19.wireOp",EDGE,"E76.0.1.3"),sQuery(id+"F19.wireOp",EDGE,"E76.0.1.4"),sQuery(id+"F19.wireOp",EDGE,"E76.0.1.5"),sQuery(id+"F19.wireOp",EDGE,"E76.1.0.0"),sQuery(id+"F19.wireOp",EDGE,"E76.1.0.1"),sQuery(id+"F19.wireOp",EDGE,"E76.1.0.2"),sQuery(id+"F19.wireOp",EDGE,"E76.1.0.3"),sQuery(id+"F19.wireOp",EDGE,"E76.1.0.4"),sQuery(id+"F19.wireOp",EDGE,"E76.1.0.5"),sQuery(id+"F19.wireOp",EDGE,"E76.1.1.0"),sQuery(id+"F19.wireOp",EDGE,"E76.1.1.1"),sQuery(id+"F19.wireOp",EDGE,"E76.1.1.2"),sQuery(id+"F19.wireOp",EDGE,"E76.1.1.3"),sQuery(id+"F19.wireOp",EDGE,"E76.1.1.4"),sQuery(id+"F19.wireOp",EDGE,"E76.1.1.5"),sQuery(id+"F19.wireOp",EDGE,"E77.0"),sQuery(id+"F19.wireOp",EDGE,"E78.0"),sQuery(id+"F19.wireOp",EDGE,"E79"),sQuery(id+"F19.wireOp",EDGE,"E80"),sQuery(id+"F19.wireOp",EDGE,"E81"),sQuery(id+"F19.wireOp",EDGE,"E82")])],"isStart":false})]});
            var sketch = newSketch(context, id + "F24", { "sketchPlane" : qUnion([Q0])});
            skLineSegment(sketch, "E106.0", {"start": v(-12.9, -39.75) * mm, "end": v(-12.9, 39.75) * mm, "construction": true});
            skLineSegment(sketch, "E107.0", {"start": v(134.81, -39.75) * mm, "end": v(134.81, 39.75) * mm, "construction": true});
            skLineSegment(sketch, "E108.rect.bottom", {"start": v(4.89, 7.62) * mm, "end": v(117.03, 7.62) * mm});
            skLineSegment(sketch, "E108.rect.top", {"start": v(4.89, -7.62) * mm, "end": v(117.03, -7.62) * mm});
            skLineSegment(sketch, "E108.rect.left", {"start": v(2.35, 5.08) * mm, "end": v(2.35, -5.08) * mm});
            skLineSegment(sketch, "E108.rect.right", {"start": v(119.57, 5.08) * mm, "end": v(119.57, -5.08) * mm});
            skPoint(sketch, "E108.rect.middle", {"position": v(60.96, 0) * mm});
            skLineSegment(sketch, "E109", {"start": v(2.35, 0) * mm, "end": v(-12.9, 0) * mm, "construction": true});
            skLineSegment(sketch, "E110", {"start": v(119.57, 0) * mm, "end": v(134.81, 0) * mm, "construction": true});
            skCircle(sketch, "E111", {"center": v(-5.27, 0) * mm, "radius": 3.18 * mm});
            skLineSegment(sketch, "E112", {"start": v(60.96, 7.62) * mm, "end": v(60.96, -7.62) * mm, "construction": true});
            skCircle(sketch, "E113.0.MirrorC", {"center": v(127.2, 0) * mm, "radius": 3.18 * mm});
            skPoint(sketch, "E114.visualSharp", {"position": v(2.35, 7.62) * mm});
            skArc(sketch, "E114.filletArc", {"start": v(4.89, 7.62) * mm, "mid": v(3.1, 6.88) * mm, "end": v(2.35, 5.08) * mm});
            skPoint(sketch, "E115.visualSharp", {"position": v(119.57, 7.62) * mm});
            skArc(sketch, "E115.filletArc", {"start": v(119.57, 5.08) * mm, "mid": v(118.83, 6.88) * mm, "end": v(117.03, 7.62) * mm});
            skPoint(sketch, "E116.visualSharp", {"position": v(119.57, -7.62) * mm});
            skArc(sketch, "E116.filletArc", {"start": v(117.03, -7.62) * mm, "mid": v(118.83, -6.88) * mm, "end": v(119.57, -5.08) * mm});
            skPoint(sketch, "E117.visualSharp", {"position": v(2.35, -7.62) * mm});
            skArc(sketch, "E117.filletArc", {"start": v(2.35, -5.08) * mm, "mid": v(3.1, -6.88) * mm, "end": v(4.89, -7.62) * mm});
            skSolve(sketch);
        }
        {
            var Q0;
            Q0=makeQuery(id+"F24.imprint","IMPRINT",FACE,{"disambiguationData":[TD([[makeQuery(id+"F24.imprint","IMPRINT",EDGE,{"derivedFrom":sQuery(id+"F24.wireOp",EDGE,"E111")}),1.0]])]});
            var Q1;
            Q1=makeQuery(id+"F24.imprint","IMPRINT",FACE,{"disambiguationData":[TD([[makeQuery(id+"F24.imprint","IMPRINT",EDGE,{"derivedFrom":sQuery(id+"F24.wireOp",EDGE,"E108.rect.bottom")}),-1.0]])]});
            var Q2;
            Q2=makeQuery(id+"F24.imprint","IMPRINT",FACE,{"disambiguationData":[TD([[makeQuery(id+"F24.imprint","IMPRINT",EDGE,{"derivedFrom":sQuery(id+"F24.wireOp",EDGE,"E113.0.MirrorC")}),-1.0]])]});
            extrude(context, id + "F25", {"entities" : qUnion([Q0, Q1, Q2]), "operationType" : NewBodyOperationType.REMOVE, "endBound" : BoundingType.THROUGH_ALL, "oppositeDirection" : true, "depth" : 25.4 * mm});
        }
    });
